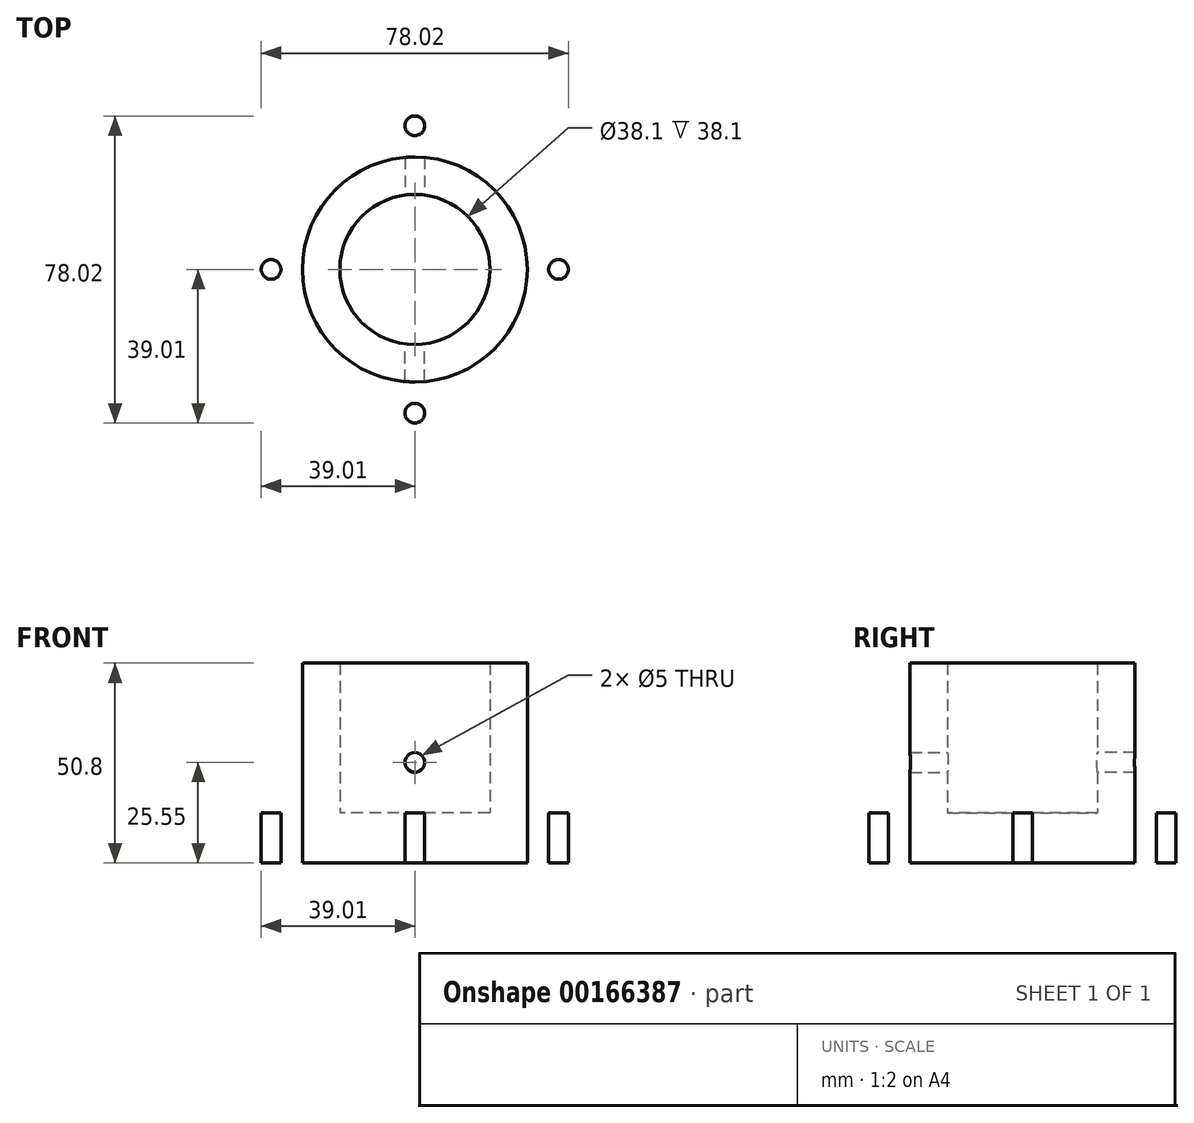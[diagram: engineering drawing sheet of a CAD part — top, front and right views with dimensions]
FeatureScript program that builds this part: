
annotation { "Feature Type Name" : "Feature", "Feature Type Description" : "" }
export const myFeature = defineFeature(function(context is Context, id is Id, definition is map)
    precondition{}
    {
        {
            var Q0;
            Q0=qCreatedBy(makeId("Top.planeOp"),FACE);
            var sketch = newSketch(context, id + "F0", { "sketchPlane" : qUnion([Q0])});
            skCircle(sketch, "E0", {"center": v(0, 0) * mm, "radius": 44.45 * mm});
            skSolve(sketch);
        }
        {
            var Q0;
            Q0=makeQuery(id+"F0.imprint","IMPRINT",FACE,{"disambiguationData":[TD([[makeQuery(id+"F0.imprint","IMPRINT",EDGE,{"derivedFrom":sQuery(id+"F0.wireOp",EDGE,"E0")}),1.0]])]});
            extrude(context, id + "F1", {"entities" : qUnion([Q0]), "depth" : 12.7 * mm});
        }
        {
            var Q0;
            Q0=makeQuery(id+"F1.opExtrude","CAP_FACE",FACE,{"disambiguationData":[OSD([sQuery(id+"F0.wireOp",EDGE,"E0")])],"isStart":false});
            var sketch = newSketch(context, id + "F2", { "sketchPlane" : qUnion([Q0])});
            skCircle(sketch, "E1", {"center": v(0, 0) * mm, "radius": 28.58 * mm});
            skCircle(sketch, "E2", {"center": v(0, 0) * mm, "radius": 19.05 * mm});
            skSolve(sketch);
        }
        {
            var Q0;
            Q0=makeQuery(id+"F2.imprint","IMPRINT",FACE,{"disambiguationData":[TD([[makeQuery(id+"F2.imprint","IMPRINT",EDGE,{"derivedFrom":sQuery(id+"F2.wireOp",EDGE,"E1")}),1.0]])]});
            extrude(context, id + "F3", {"entities" : qUnion([Q0]), "operationType" : NewBodyOperationType.ADD, "depth" : 38.1 * mm});
        }
        {
            var Q0;
            {var subQ0=sQuery(id+"F0.wireOp",EDGE,"E0");Q0=makeQuery(id+"F3.boolean.opBoolean","SPLIT",FACE,{"disambiguationData":[TD([makeQuery(id+"F1.opExtrude","SWEPT_FACE",FACE,{"disambiguationData":[OSD([subQ0])]})])],"derivedFrom":makeQuery(id+"F1.opExtrude","CAP_FACE",FACE,{"disambiguationData":[OSD([subQ0])],"isStart":false})});}
            var sketch = newSketch(context, id + "F4", { "sketchPlane" : qUnion([Q0])});
            skLineSegment(sketch, "E3", {"start": v(-28.58, 0) * mm, "end": v(-44.45, 0) * mm});
            skLineSegment(sketch, "E4", {"start": v(-44.45, 0) * mm, "end": v(-36.51, 0) * mm});
            skLineSegment(sketch, "E5", {"start": v(28.58, 0) * mm, "end": v(44.45, 0) * mm});
            skLineSegment(sketch, "E6", {"start": v(44.45, 0) * mm, "end": v(36.51, 0) * mm});
            skLineSegment(sketch, "E7", {"start": v(0, -28.58) * mm, "end": v(0, -44.45) * mm});
            skLineSegment(sketch, "E8", {"start": v(0, -44.45) * mm, "end": v(0, -36.51) * mm});
            skLineSegment(sketch, "E9", {"start": v(0, 28.58) * mm, "end": v(0, 44.45) * mm});
            skLineSegment(sketch, "E10", {"start": v(0, 44.45) * mm, "end": v(0, 36.51) * mm});
            skCircle(sketch, "E11", {"center": v(-36.51, 0) * mm, "radius": 2.5 * mm});
            skCircle(sketch, "E12", {"center": v(36.51, 0) * mm, "radius": 2.5 * mm});
            skCircle(sketch, "E13", {"center": v(0, -36.51) * mm, "radius": 2.5 * mm});
            skCircle(sketch, "E14", {"center": v(0, 36.51) * mm, "radius": 2.5 * mm});
            skPoint(sketch, "E15.start.orphan", {"position": v(0, 0) * mm});
            skSolve(sketch);
        }
        {
            var Q0;
            {var subQ0=sQuery(id+"F4.wireOp",EDGE,"E8");var subQ1=sQuery(id+"F4.wireOp",EDGE,"E7");var subQ2=makeQuery(id+"F4.imprint","INTERSECT",VERTEX,{"derivedFrom":[subQ1,subQ0]});Q0=makeQuery(id+"F4.imprint","IMPRINT",FACE,{"disambiguationData":[TD([[makeQuery(id+"F4.imprint","IMPRINT",EDGE,{"disambiguationData":[TD([[subQ2,1.0]])],"derivedFrom":subQ1}),-1.0]])]});}
            var Q1;
            {var subQ0=sQuery(id+"F4.wireOp",EDGE,"E8");var subQ1=sQuery(id+"F4.wireOp",EDGE,"E7");var subQ2=makeQuery(id+"F4.imprint","INTERSECT",VERTEX,{"derivedFrom":[subQ1,subQ0]});Q1=makeQuery(id+"F4.imprint","IMPRINT",FACE,{"disambiguationData":[TD([[makeQuery(id+"F4.imprint","IMPRINT",EDGE,{"disambiguationData":[TD([[subQ2,1.0]])],"derivedFrom":subQ1}),1.0]])]});}
            var Q2;
            {var subQ0=sQuery(id+"F4.wireOp",EDGE,"E4");var subQ1=sQuery(id+"F4.wireOp",EDGE,"E3");var subQ2=makeQuery(id+"F4.imprint","INTERSECT",VERTEX,{"derivedFrom":[subQ1,subQ0]});Q2=makeQuery(id+"F4.imprint","IMPRINT",FACE,{"disambiguationData":[TD([[makeQuery(id+"F4.imprint","IMPRINT",EDGE,{"disambiguationData":[TD([[subQ2,1.0]])],"derivedFrom":subQ1}),1.0]])]});}
            var Q3;
            {var subQ0=sQuery(id+"F4.wireOp",EDGE,"E4");var subQ1=sQuery(id+"F4.wireOp",EDGE,"E3");var subQ2=makeQuery(id+"F4.imprint","INTERSECT",VERTEX,{"derivedFrom":[subQ1,subQ0]});Q3=makeQuery(id+"F4.imprint","IMPRINT",FACE,{"disambiguationData":[TD([[makeQuery(id+"F4.imprint","IMPRINT",EDGE,{"disambiguationData":[TD([[subQ2,1.0]])],"derivedFrom":subQ1}),-1.0]])]});}
            var Q4;
            {var subQ0=sQuery(id+"F4.wireOp",EDGE,"E10");var subQ1=sQuery(id+"F4.wireOp",EDGE,"E9");var subQ2=makeQuery(id+"F4.imprint","INTERSECT",VERTEX,{"derivedFrom":[subQ1,subQ0]});Q4=makeQuery(id+"F4.imprint","IMPRINT",FACE,{"disambiguationData":[TD([[makeQuery(id+"F4.imprint","IMPRINT",EDGE,{"disambiguationData":[TD([[subQ2,1.0]])],"derivedFrom":subQ1}),1.0]])]});}
            var Q5;
            {var subQ0=sQuery(id+"F4.wireOp",EDGE,"E6");var subQ1=sQuery(id+"F4.wireOp",EDGE,"E5");var subQ2=makeQuery(id+"F4.imprint","INTERSECT",VERTEX,{"derivedFrom":[subQ1,subQ0]});Q5=makeQuery(id+"F4.imprint","IMPRINT",FACE,{"disambiguationData":[TD([[makeQuery(id+"F4.imprint","IMPRINT",EDGE,{"disambiguationData":[TD([[subQ2,1.0]])],"derivedFrom":subQ1}),1.0]])]});}
            var Q6;
            {var subQ0=sQuery(id+"F4.wireOp",EDGE,"E6");var subQ1=sQuery(id+"F4.wireOp",EDGE,"E5");var subQ2=makeQuery(id+"F4.imprint","INTERSECT",VERTEX,{"derivedFrom":[subQ1,subQ0]});Q6=makeQuery(id+"F4.imprint","IMPRINT",FACE,{"disambiguationData":[TD([[makeQuery(id+"F4.imprint","IMPRINT",EDGE,{"disambiguationData":[TD([[subQ2,1.0]])],"derivedFrom":subQ1}),-1.0]])]});}
            var Q7;
            {var subQ0=sQuery(id+"F4.wireOp",EDGE,"E10");var subQ1=sQuery(id+"F4.wireOp",EDGE,"E9");var subQ2=makeQuery(id+"F4.imprint","INTERSECT",VERTEX,{"derivedFrom":[subQ1,subQ0]});Q7=makeQuery(id+"F4.imprint","IMPRINT",FACE,{"disambiguationData":[TD([[makeQuery(id+"F4.imprint","IMPRINT",EDGE,{"disambiguationData":[TD([[subQ2,1.0]])],"derivedFrom":subQ1}),-1.0]])]});}
            extrude(context, id + "F5", {"entities" : qUnion([Q0, Q1, Q2, Q3, Q4, Q5, Q6, Q7]), "operationType" : NewBodyOperationType.REMOVE, "endBound" : BoundingType.THROUGH_ALL, "oppositeDirection" : true, "depth" : 25 * mm});
        }
        {
            var Q0;
            Q0=qCreatedBy(makeId("Front.planeOp"),FACE);
            var sketch = newSketch(context, id + "F6", { "sketchPlane" : qUnion([Q0])});
            skPoint(sketch, "E16", {"position": v(0, 25.55) * mm});
            skCircle(sketch, "E17", {"center": v(0, 25.55) * mm, "radius": 2.5 * mm});
            skSolve(sketch);
        }
        {
            var Q0;
            Q0 = qSketchRegion(id + "F6", true);
            extrude(context, id + "F7", {"entities" : qUnion([Q0]), "operationType" : NewBodyOperationType.REMOVE, "endBound" : BoundingType.THROUGH_ALL, "oppositeDirection" : true, "depth" : 25 * mm});
        }
        {
            var Q0;
            Q0 = qSketchRegion(id + "F6", true);
            extrude(context, id + "F8", {"entities" : qUnion([Q0]), "operationType" : NewBodyOperationType.REMOVE, "endBound" : BoundingType.THROUGH_ALL, "depth" : 25 * mm});
        }
    });
